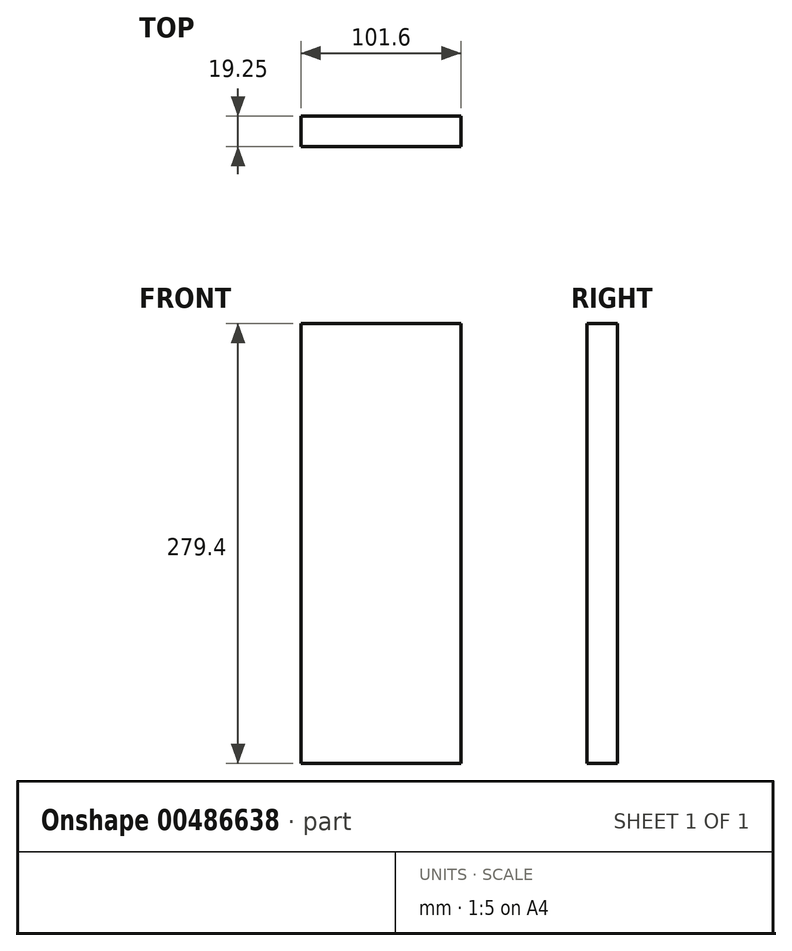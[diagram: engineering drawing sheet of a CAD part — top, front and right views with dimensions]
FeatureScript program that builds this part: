
annotation { "Feature Type Name" : "Feature", "Feature Type Description" : "" }
export const myFeature = defineFeature(function(context is Context, id is Id, definition is map)
    precondition{}
    {
        {
            var Q0;
            Q0=qCreatedBy(makeId("Front.planeOp"),FACE);
            var sketch = newSketch(context, id + "F0", { "sketchPlane" : qUnion([Q0])});
            skLineSegment(sketch, "E0", {"start": v(-61.1, 279.4) * mm, "end": v(-61.1, 0) * mm});
            skLineSegment(sketch, "E1", {"start": v(-61.1, 0) * mm, "end": v(40.5, 0) * mm});
            skLineSegment(sketch, "E2", {"start": v(40.5, 0) * mm, "end": v(40.5, 279.4) * mm});
            skLineSegment(sketch, "E3", {"start": v(40.5, 279.4) * mm, "end": v(-61.1, 279.4) * mm});
            skSolve(sketch);
        }
        {
            var Q0;
            Q0 = qSketchRegion(id + "F0", true);
            extrude(context, id + "F1", {"entities" : qUnion([Q0]), "depth" : 19.25 * mm, "offsetDistance" : 25.4 * mm});
        }
    });
